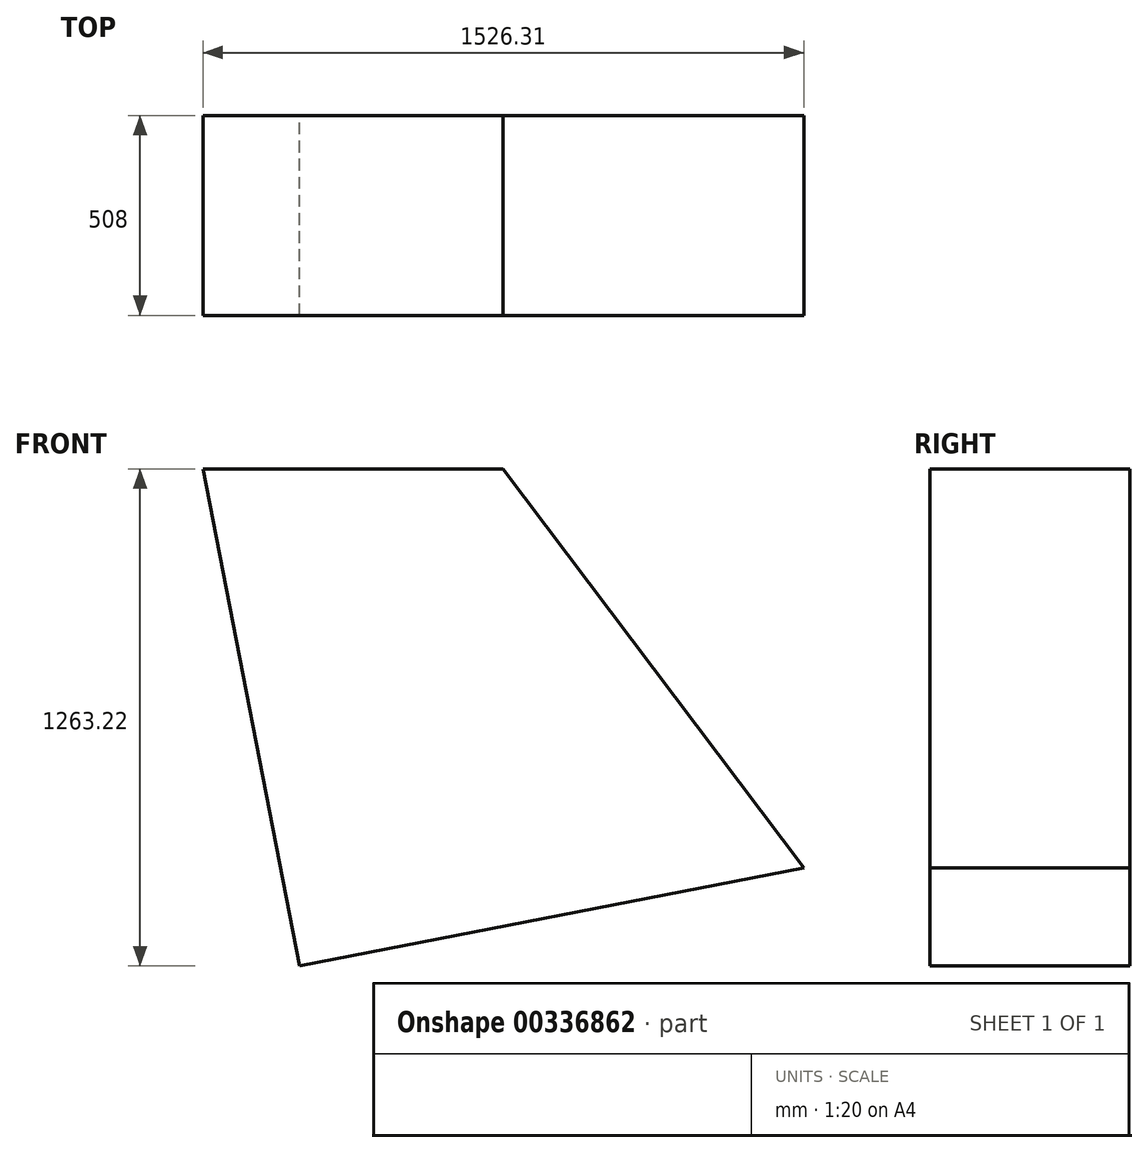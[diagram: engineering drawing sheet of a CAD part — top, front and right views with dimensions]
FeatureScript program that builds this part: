
annotation { "Feature Type Name" : "Feature", "Feature Type Description" : "" }
export const myFeature = defineFeature(function(context is Context, id is Id, definition is map)
    precondition{}
    {
        {
            var Q0;
            Q0=qCreatedBy(makeId("Front.planeOp"),FACE);
            var sketch = newSketch(context, id + "F0", { "sketchPlane" : qUnion([Q0])});
            skLineSegment(sketch, "E0", {"start": v(-551.18, 389.64) * mm, "end": v(210.82, 389.64) * mm});
            skLineSegment(sketch, "E1", {"start": v(210.82, 389.64) * mm, "end": v(975.13, -624.63) * mm});
            skLineSegment(sketch, "E2", {"start": v(975.13, -624.63) * mm, "end": v(-305.63, -873.58) * mm});
            skLineSegment(sketch, "E3", {"start": v(-305.63, -873.58) * mm, "end": v(-551.18, 389.64) * mm});
            skSolve(sketch);
        }
        {
            var Q0;
            Q0 = qSketchRegion(id + "F0", true);
            extrude(context, id + "F1", {"entities" : qUnion([Q0]), "depth" : 508 * mm});
        }
    });
